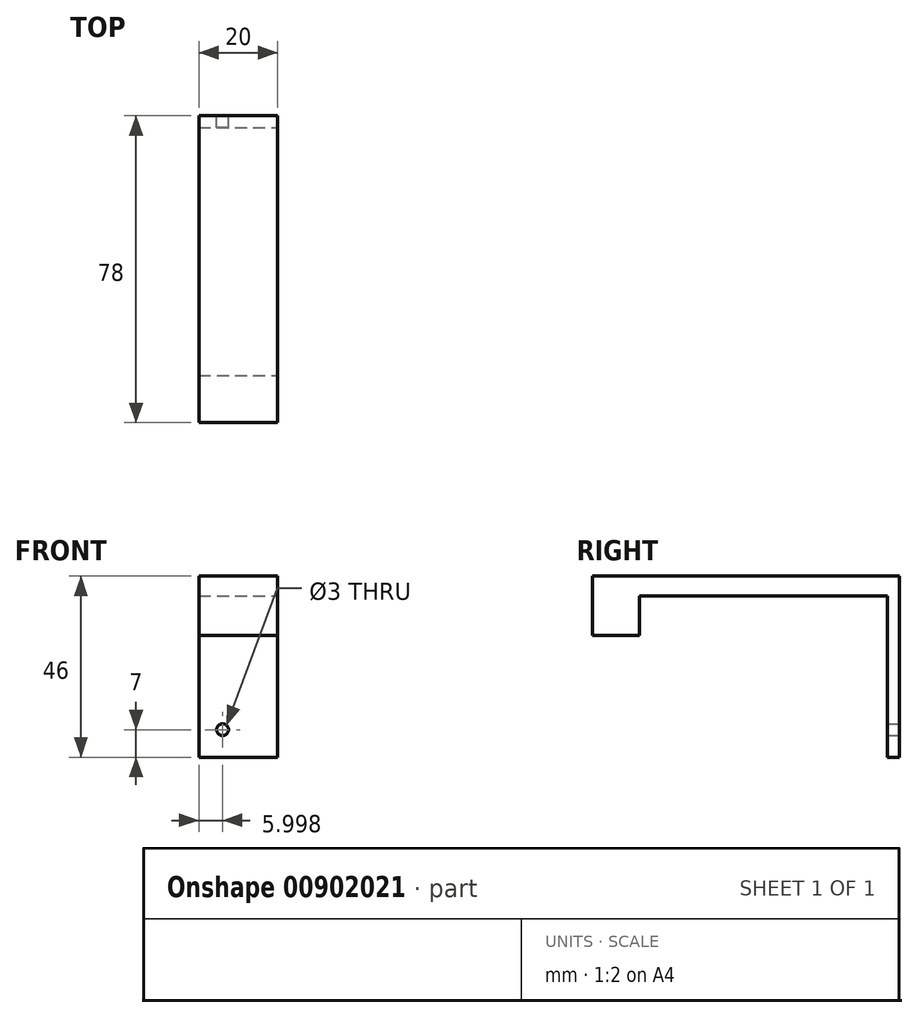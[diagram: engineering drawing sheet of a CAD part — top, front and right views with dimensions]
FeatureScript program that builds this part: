
annotation { "Feature Type Name" : "Feature", "Feature Type Description" : "" }
export const myFeature = defineFeature(function(context is Context, id is Id, definition is map)
    precondition{}
    {
        {
            var Q0;
            Q0=qCreatedBy(makeId("Top.planeOp"),FACE);
            var sketch = newSketch(context, id + "F0", { "sketchPlane" : qUnion([Q0])});
            skLineSegment(sketch, "E0.bottom", {"start": v(-11.32, 38.07) * mm, "end": v(8.68, 38.07) * mm});
            skLineSegment(sketch, "E0.top", {"start": v(-11.32, -24.93) * mm, "end": v(8.68, -24.93) * mm});
            skLineSegment(sketch, "E0.left", {"start": v(-11.32, 38.07) * mm, "end": v(-11.32, -24.93) * mm});
            skLineSegment(sketch, "E0.right", {"start": v(8.68, 38.07) * mm, "end": v(8.68, -24.93) * mm});
            skSolve(sketch);
        }
        {
            var Q0;
            Q0 = qSketchRegion(id + "F0", true);
            extrude(context, id + "F1", {"entities" : qUnion([Q0]), "endBound" : BoundingType.SYMMETRIC, "depth" : 5 * mm, "offsetDistance" : 25 * mm});
        }
        {
            var Q0;
            Q0=makeQuery(id+"F1.opExtrude","SWEPT_FACE",FACE,{"disambiguationData":[OSD([sQuery(id+"F0.wireOp",EDGE,"E0.top")])]});
            var sketch = newSketch(context, id + "F2", { "sketchPlane" : qUnion([Q0])});
            skLineSegment(sketch, "E1.bottom", {"start": v(-11.32, 2.5) * mm, "end": v(8.68, 2.5) * mm});
            skLineSegment(sketch, "E1.top", {"start": v(-11.32, -12.5) * mm, "end": v(8.68, -12.5) * mm});
            skLineSegment(sketch, "E1.left", {"start": v(-11.32, 2.5) * mm, "end": v(-11.32, -12.5) * mm});
            skLineSegment(sketch, "E1.right", {"start": v(8.68, 2.5) * mm, "end": v(8.68, -12.5) * mm});
            skSolve(sketch);
        }
        {
            var Q0;
            Q0 = qSketchRegion(id + "F2", true);
            extrude(context, id + "F3", {"entities" : qUnion([Q0]), "operationType" : NewBodyOperationType.ADD, "depth" : 12 * mm, "offsetDistance" : 25 * mm});
        }
        {
            var Q0;
            Q0=makeQuery(id+"F1.opExtrude","SWEPT_FACE",FACE,{"disambiguationData":[OSD([sQuery(id+"F0.wireOp",EDGE,"E0.bottom")])]});
            var sketch = newSketch(context, id + "F4", { "sketchPlane" : qUnion([Q0])});
            skLineSegment(sketch, "E2.bottom", {"start": v(-8.68, 2.5) * mm, "end": v(11.32, 2.5) * mm});
            skLineSegment(sketch, "E2.top", {"start": v(-8.68, -43.5) * mm, "end": v(11.32, -43.5) * mm});
            skLineSegment(sketch, "E2.left", {"start": v(-8.68, 2.5) * mm, "end": v(-8.68, -43.5) * mm});
            skLineSegment(sketch, "E2.right", {"start": v(11.32, 2.5) * mm, "end": v(11.32, -43.5) * mm});
            skSolve(sketch);
        }
        {
            var Q0;
            Q0 = qSketchRegion(id + "F4", true);
            extrude(context, id + "F5", {"entities" : qUnion([Q0]), "operationType" : NewBodyOperationType.ADD, "depth" : 3 * mm, "offsetDistance" : 25 * mm});
        }
        {
            var Q0;
            Q0=makeQuery(id+"F5.opExtrude","CAP_FACE",FACE,{"disambiguationData":[OSD([sQuery(id+"F4.wireOp",EDGE,"E2.bottom"),sQuery(id+"F4.wireOp",EDGE,"E2.top"),sQuery(id+"F4.wireOp",EDGE,"E2.left"),sQuery(id+"F4.wireOp",EDGE,"E2.right")])],"isStart":false});
            var sketch = newSketch(context, id + "F6", { "sketchPlane" : qUnion([Q0])});
            skCircle(sketch, "E3", {"center": v(5.32, -36.5) * mm, "radius": 1.5 * mm});
            skSolve(sketch);
        }
        {
            var Q0;
            Q0 = qSketchRegion(id + "F6", true);
            extrude(context, id + "F7", {"entities" : qUnion([Q0]), "operationType" : NewBodyOperationType.REMOVE, "oppositeDirection" : true, "depth" : 25 * mm, "offsetDistance" : 25 * mm});
        }
    });
